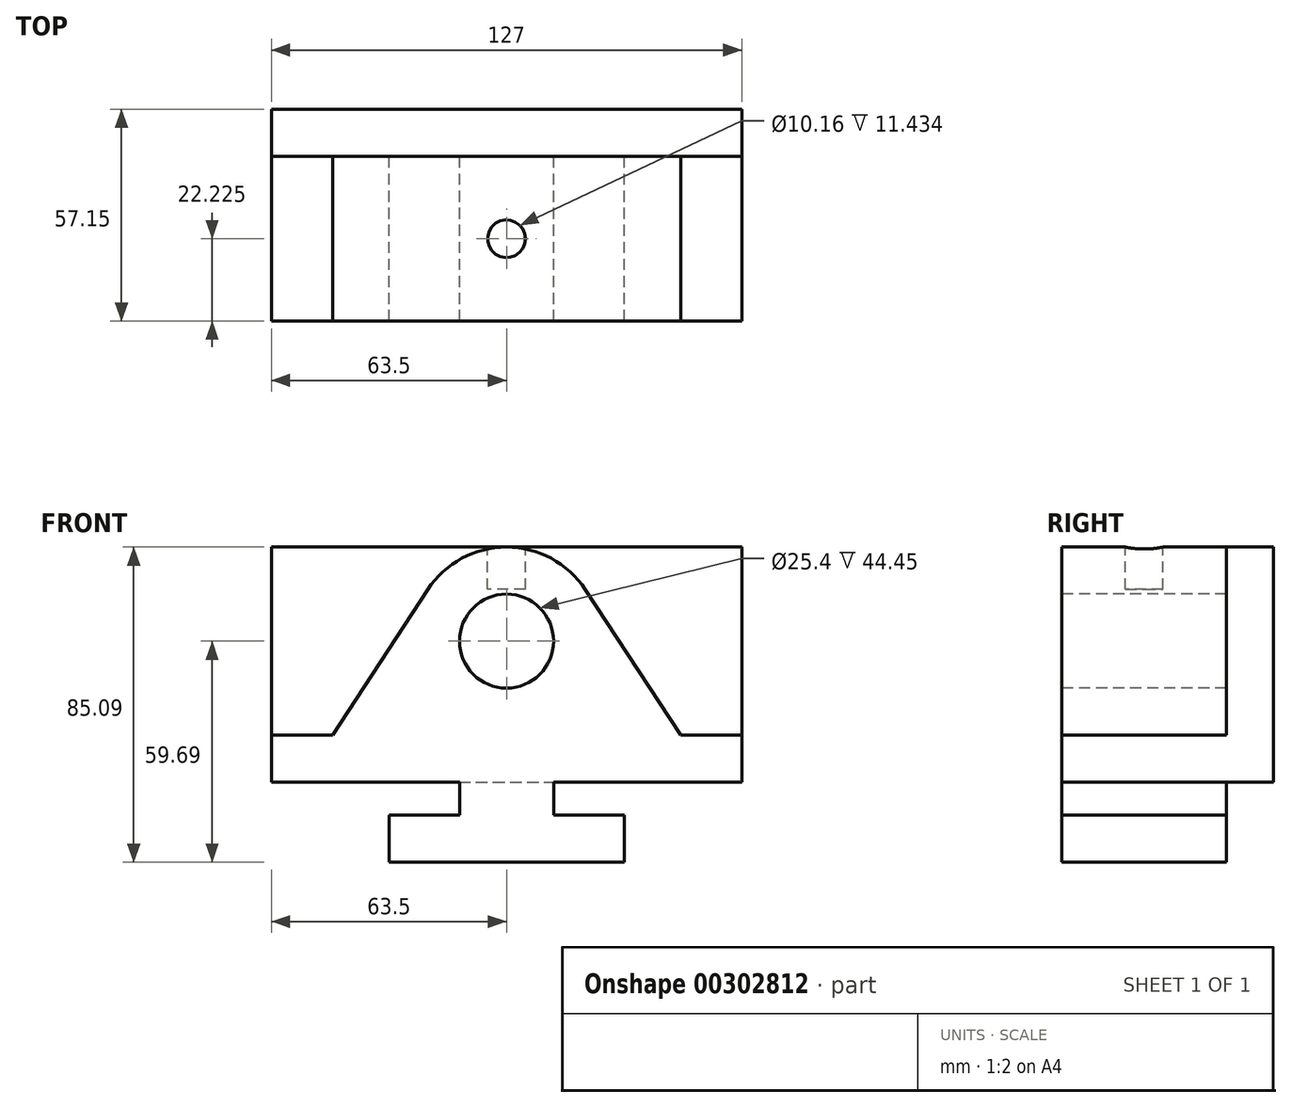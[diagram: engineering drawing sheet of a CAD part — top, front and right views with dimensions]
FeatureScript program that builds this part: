
annotation { "Feature Type Name" : "Feature", "Feature Type Description" : "" }
export const myFeature = defineFeature(function(context is Context, id is Id, definition is map)
    precondition{}
    {
        {
            var Q0;
            Q0=qCreatedBy(makeId("Front.planeOp"),FACE);
            var sketch = newSketch(context, id + "F0", { "sketchPlane" : qUnion([Q0])});
            skLineSegment(sketch, "E0", {"start": v(0, 0) * mm, "end": v(63.5, 0) * mm});
            skLineSegment(sketch, "E1", {"start": v(63.5, 0) * mm, "end": v(63.5, 12.7) * mm});
            skLineSegment(sketch, "E2", {"start": v(0, 0) * mm, "end": v(0, 12.7) * mm});
            skLineSegment(sketch, "E3", {"start": v(0, 12.7) * mm, "end": v(19.05, 12.7) * mm});
            skLineSegment(sketch, "E4", {"start": v(19.05, 12.7) * mm, "end": v(19.05, 21.6) * mm});
            skLineSegment(sketch, "E5", {"start": v(19.05, 21.59) * mm, "end": v(-31.75, 21.59) * mm});
            skLineSegment(sketch, "E6", {"start": v(-31.75, 21.59) * mm, "end": v(-31.75, 34.3) * mm});
            skLineSegment(sketch, "E7", {"start": v(63.5, 12.7) * mm, "end": v(44.45, 12.7) * mm});
            skLineSegment(sketch, "E8", {"start": v(44.45, 12.7) * mm, "end": v(44.45, 21.59) * mm});
            skLineSegment(sketch, "E9", {"start": v(44.45, 21.59) * mm, "end": v(95.25, 21.59) * mm});
            skLineSegment(sketch, "E10", {"start": v(95.25, 21.59) * mm, "end": v(95.25, 34.3) * mm});
            skLineSegment(sketch, "E11", {"start": v(-31.75, 34.3) * mm, "end": v(-15.24, 34.3) * mm});
            skLineSegment(sketch, "E12", {"start": v(95.25, 34.3) * mm, "end": v(78.74, 34.3) * mm});
            skLineSegment(sketch, "E13", {"start": v(31.75, 0) * mm, "end": v(31.75, 85.1) * mm, "construction": true});
            skLineSegment(sketch, "E14", {"start": v(-15.24, 34.3) * mm, "end": v(10.5, 73.6) * mm});
            skLineSegment(sketch, "E15", {"start": v(78.74, 34.29) * mm, "end": v(53, 73.6) * mm});
            skArc(sketch, "E16", {"start": v(53, 73.6) * mm, "mid": v(31.75, 85.1) * mm, "end": v(10.5, 73.6) * mm});
            skSolve(sketch);
        }
        {
            var Q0;
            Q0 = qSketchRegion(id + "F0", true);
            extrude(context, id + "F1", {"entities" : qUnion([Q0]), "depth" : 44.45 * mm});
        }
        {
            var Q0;
            Q0=makeQuery(id+"F1.opExtrude","CAP_FACE",FACE,{"disambiguationData":[OSD([sQuery(id+"F0.wireOp",EDGE,"E0"),sQuery(id+"F0.wireOp",EDGE,"E1"),sQuery(id+"F0.wireOp",EDGE,"E2"),sQuery(id+"F0.wireOp",EDGE,"E3"),sQuery(id+"F0.wireOp",EDGE,"E4"),sQuery(id+"F0.wireOp",EDGE,"E5"),sQuery(id+"F0.wireOp",EDGE,"E6"),sQuery(id+"F0.wireOp",EDGE,"E7"),sQuery(id+"F0.wireOp",EDGE,"E8"),sQuery(id+"F0.wireOp",EDGE,"E9"),sQuery(id+"F0.wireOp",EDGE,"E10"),sQuery(id+"F0.wireOp",EDGE,"E11"),sQuery(id+"F0.wireOp",EDGE,"E12"),sQuery(id+"F0.wireOp",EDGE,"E14"),sQuery(id+"F0.wireOp",EDGE,"E15"),sQuery(id+"F0.wireOp",EDGE,"E16")])],"isStart":false});
            var sketch = newSketch(context, id + "F2", { "sketchPlane" : qUnion([Q0])});
            skCircle(sketch, "E17", {"center": v(31.75, 59.69) * mm, "radius": 12.7 * mm});
            skSolve(sketch);
        }
        {
            var Q0;
            Q0 = qSketchRegion(id + "F2", true);
            extrude(context, id + "F3", {"entities" : qUnion([Q0]), "operationType" : NewBodyOperationType.REMOVE, "oppositeDirection" : true, "depth" : 45.72 * mm});
        }
        {
            var Q0;
            Q0=makeQuery(id+"F1.opExtrude","SWEPT_FACE",FACE,{"disambiguationData":[OSD([sQuery(id+"F0.wireOp",EDGE,"E10")])]});
            var sketch = newSketch(context, id + "F4", { "sketchPlane" : qUnion([Q0])});
            skLineSegment(sketch, "E18", {"start": v(0, 21.59) * mm, "end": v(12.7, 21.59) * mm});
            skLineSegment(sketch, "E19", {"start": v(12.7, 21.59) * mm, "end": v(12.7, 85.1) * mm});
            skLineSegment(sketch, "E20", {"start": v(0, 85.1) * mm, "end": v(12.7, 85.1) * mm});
            skLineSegment(sketch, "E21", {"start": v(0, 85.1) * mm, "end": v(0, 21.6) * mm});
            skSolve(sketch);
        }
        {
            var Q0;
            Q0 = qSketchRegion(id + "F4", true);
            extrude(context, id + "F5", {"entities" : qUnion([Q0]), "operationType" : NewBodyOperationType.ADD, "oppositeDirection" : true, "depth" : 127 * mm});
        }
        {
            var Q0;
            Q0=makeQuery(id+"F5.opExtrude","SWEPT_FACE",FACE,{"disambiguationData":[OSD([sQuery(id+"F4.wireOp",EDGE,"E20")])]});
            var sketch = newSketch(context, id + "F6", { "sketchPlane" : qUnion([Q0])});
            skCircle(sketch, "E22", {"center": v(31.75, -22.23) * mm, "radius": 5.08 * mm});
            skSolve(sketch);
        }
        {
            var Q0;
            Q0 = qSketchRegion(id + "F6", true);
            extrude(context, id + "F7", {"entities" : qUnion([Q0]), "operationType" : NewBodyOperationType.REMOVE, "oppositeDirection" : true, "depth" : 11.43 * mm});
        }
    });
